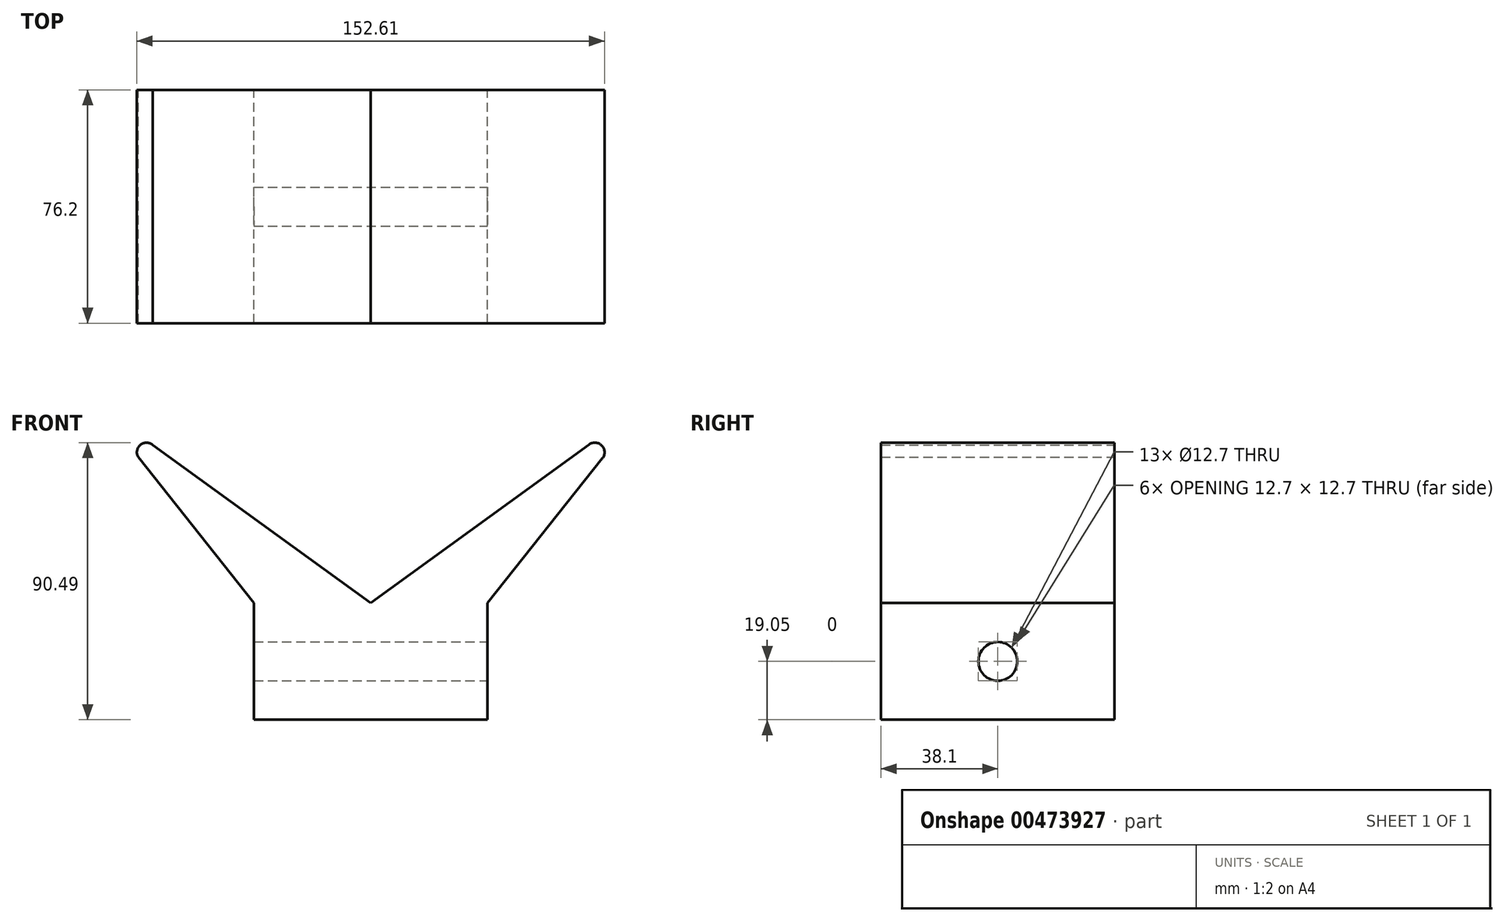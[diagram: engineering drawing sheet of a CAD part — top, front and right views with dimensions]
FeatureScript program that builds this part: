
annotation { "Feature Type Name" : "Feature", "Feature Type Description" : "" }
export const myFeature = defineFeature(function(context is Context, id is Id, definition is map)
    precondition{}
    {
        {
            var Q0;
            Q0=qCreatedBy(makeId("Front.planeOp"),FACE);
            var sketch = newSketch(context, id + "F0", { "sketchPlane" : qUnion([Q0])});
            skLineSegment(sketch, "E0", {"start": v(0, 0) * mm, "end": v(76.2, 0) * mm});
            skLineSegment(sketch, "E1", {"start": v(0, 0) * mm, "end": v(0, 38.1) * mm});
            skLineSegment(sketch, "E2", {"start": v(76.2, 38.1) * mm, "end": v(76.2, 0) * mm});
            skCircle(sketch, "E3", {"center": v(-35.03, 87.31) * mm, "radius": 3.18 * mm});
            skCircle(sketch, "E4", {"center": v(111.24, 87.31) * mm, "radius": 3.18 * mm});
            skLineSegment(sketch, "E5", {"start": v(-37.77, 85.72) * mm, "end": v(0, 38.1) * mm});
            skLineSegment(sketch, "E6", {"start": v(-33.01, 89.77) * mm, "end": v(38.1, 38.1) * mm});
            skLineSegment(sketch, "E7", {"start": v(38.1, 38.1) * mm, "end": v(109.37, 89.88) * mm});
            skLineSegment(sketch, "E8", {"start": v(76.2, 38.1) * mm, "end": v(113.72, 85.34) * mm});
            skLineSegment(sketch, "E9", {"start": v(38.1, 38.1) * mm, "end": v(38.1, 0) * mm});
            skLineSegment(sketch, "E10", {"start": v(0, 38.1) * mm, "end": v(38.1, 38.1) * mm, "construction": true});
            skLineSegment(sketch, "E11", {"start": v(76.2, 38.1) * mm, "end": v(38.1, 38.1) * mm, "construction": true});
            skSolve(sketch);
        }
        {
            var Q0;
            {var subQ4=sQuery(id+"F0.wireOp",EDGE,"E1");Q0=makeQuery(id+"F0.imprint","IMPRINT",FACE,{"disambiguationData":[TD([[makeQuery(id+"F0.imprint","IMPRINT",EDGE,{"derivedFrom":subQ4}),-1.0]])]});}
            var Q1;
            {var subQ1=sQuery(id+"F0.wireOp",EDGE,"E2");Q1=makeQuery(id+"F0.imprint","IMPRINT",FACE,{"disambiguationData":[TD([[makeQuery(id+"F0.imprint","IMPRINT",EDGE,{"derivedFrom":subQ1}),-1.0]])]});}
            var Q2;
            {var subQ0=sQuery(id+"F0.wireOp",EDGE,"E4");var subQ1=makeQuery(id+"F0.imprint","INTERSECT",VERTEX,{"derivedFrom":[subQ0,sQuery(id+"F0.wireOp",EDGE,"E7")]});Q2=makeQuery(id+"F0.imprint","IMPRINT",FACE,{"disambiguationData":[TD([[makeQuery(id+"F0.imprint","IMPRINT",EDGE,{"disambiguationData":[TD([[subQ1,-1.0]])],"derivedFrom":subQ0}),1.0]])]});}
            var Q3;
            {var subQ0=sQuery(id+"F0.wireOp",EDGE,"E5");var subQ1=sQuery(id+"F0.wireOp",EDGE,"E3");var subQ2=makeQuery(id+"F0.imprint","INTERSECT",VERTEX,{"disambiguationData":[OD(0.0)],"derivedFrom":[subQ1,subQ0]});Q3=makeQuery(id+"F0.imprint","IMPRINT",FACE,{"disambiguationData":[TD([[makeQuery(id+"F0.imprint","IMPRINT",EDGE,{"disambiguationData":[TD([[subQ2,1.0]])],"derivedFrom":subQ1}),1.0]])]});}
            extrude(context, id + "F1", {"entities" : qUnion([Q0, Q1, Q2, Q3]), "depth" : 76.2 * mm});
        }
        {
            var Q0;
            Q0=makeQuery(id+"F1.opExtrude","SWEPT_FACE",FACE,{"disambiguationData":[OSD([sQuery(id+"F0.wireOp",EDGE,"E2")])]});
            cPlane(context, id + "F2", {"entities" : qUnion([Q0]), "cplaneType" : CPlaneType.OFFSET, "offset" : 25.4 * mm, "width" : 152.4 * mm, "height" : 152.4 * mm});
        }
        {
            var Q0;
            Q0=qCreatedBy(id+"F2.planeOp",FACE);
            var sketch = newSketch(context, id + "F3", { "sketchPlane" : qUnion([Q0])});
            skCircle(sketch, "E12", {"center": v(-38.1, 19.05) * mm, "radius": 6.35 * mm});
            skSolve(sketch);
        }
        {
            var Q0;
            Q0=sQuery(id+"F3.wireOp",VERTEX,"E12.center");
            var Q1;
            Q1=makeQuery(id+"F1.opExtrude","SWEPT_BODY",BODY,{"disambiguationData":[OSD([sQuery(id+"F0.wireOp",EDGE,"E0"),sQuery(id+"F0.wireOp",EDGE,"E1"),sQuery(id+"F0.wireOp",EDGE,"E2"),sQuery(id+"F0.wireOp",EDGE,"E3"),sQuery(id+"F0.wireOp",EDGE,"E4"),sQuery(id+"F0.wireOp",EDGE,"E5"),sQuery(id+"F0.wireOp",EDGE,"E6"),sQuery(id+"F0.wireOp",EDGE,"E7"),sQuery(id+"F0.wireOp",EDGE,"E8")])]});
            hole(context, id + "F4", {"style" : HoleStyle.SIMPLE, "endStyle" : HoleEndStyle.THROUGH, "holeDiameter" : 12.7 * mm, "isTappedThrough" : true, "tappedDepth" : 12.7 * mm, "tapClearance" : 3, "locations" : qUnion([Q0]), "scope" : qUnion([Q1])});
        }
    });
